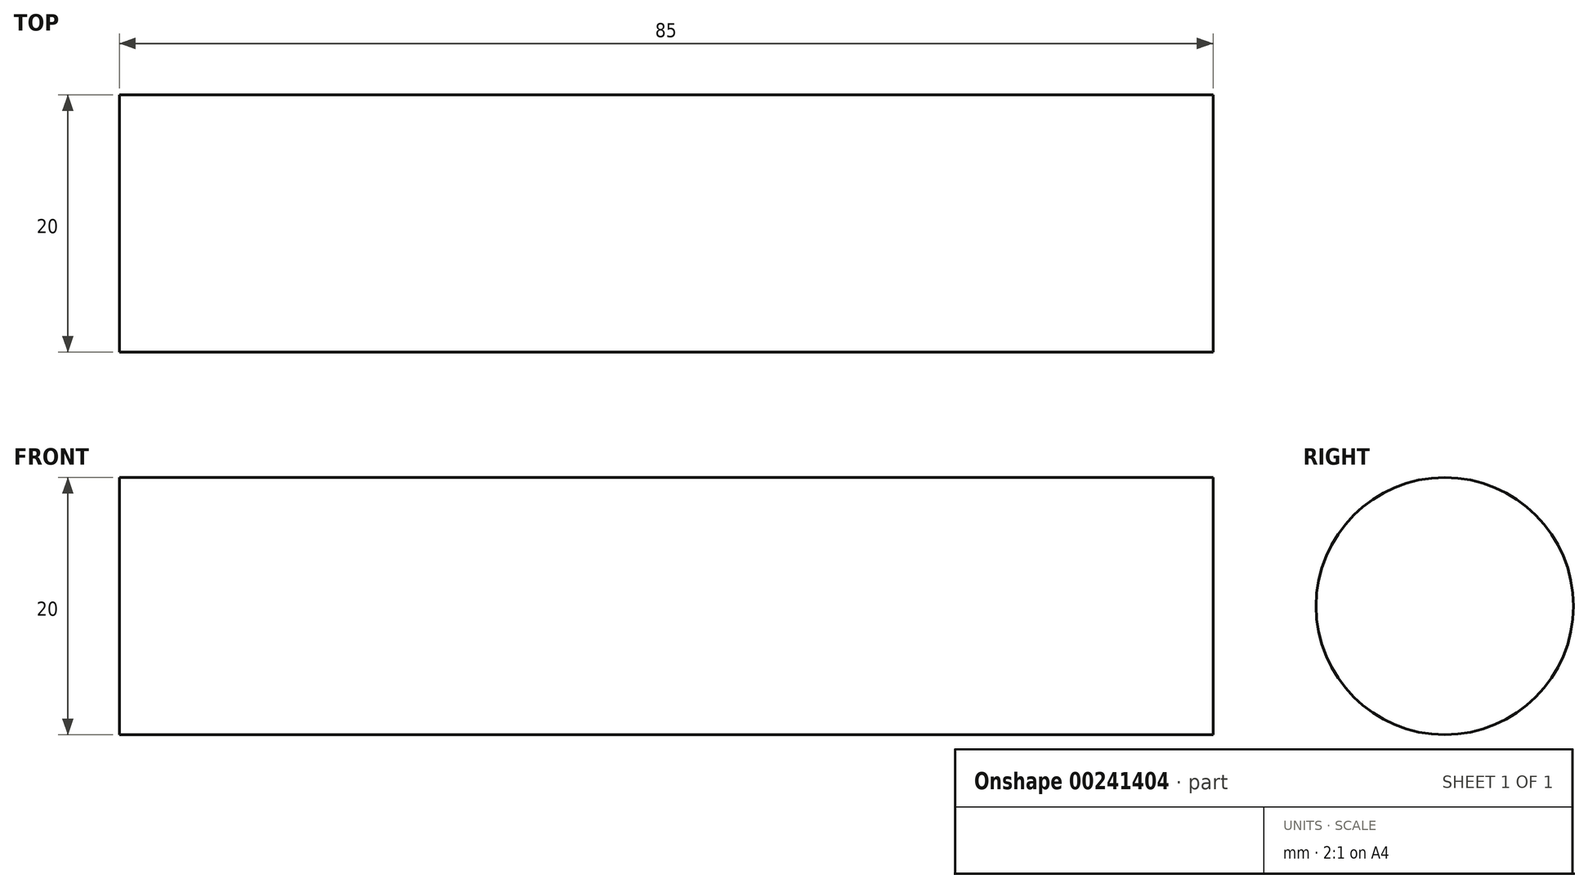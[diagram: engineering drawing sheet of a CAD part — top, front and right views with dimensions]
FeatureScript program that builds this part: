
annotation { "Feature Type Name" : "Feature", "Feature Type Description" : "" }
export const myFeature = defineFeature(function(context is Context, id is Id, definition is map)
    precondition{}
    {
        {
            var Q0;
            Q0=qCreatedBy(makeId("Right.planeOp"),FACE);
            var sketch = newSketch(context, id + "F0", { "sketchPlane" : qUnion([Q0])});
            skCircle(sketch, "E0", {"center": v(0, 0) * mm, "radius": 10 * mm});
            skSolve(sketch);
        }
        {
            var Q0;
            Q0 = qSketchRegion(id + "F0", true);
            extrude(context, id + "F1", {"entities" : qUnion([Q0]), "endBound" : BoundingType.SYMMETRIC, "depth" : 85 * mm});
        }
    });
